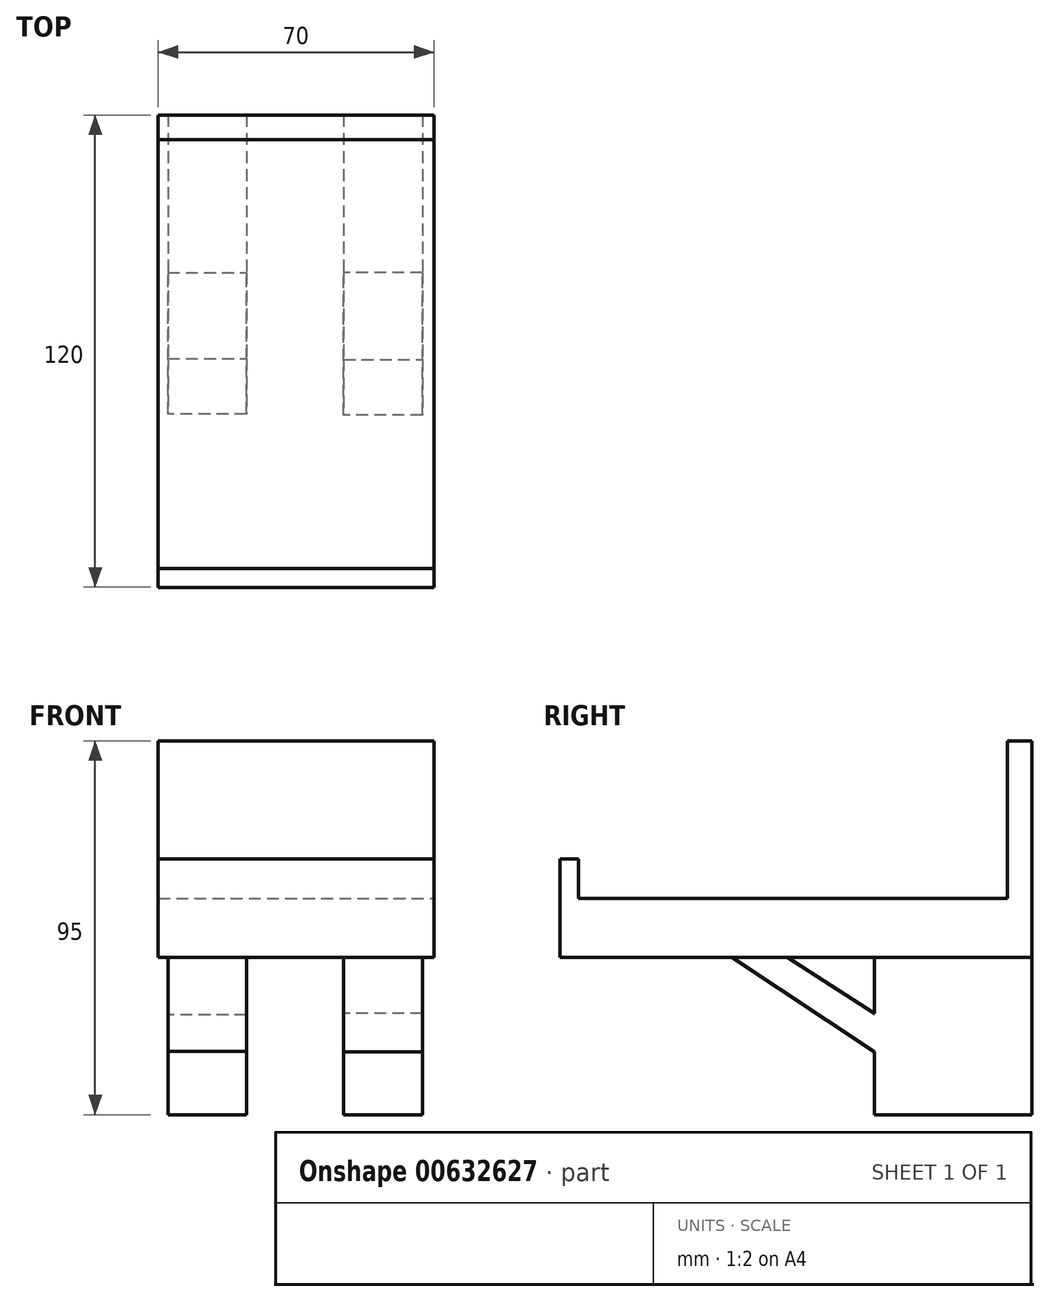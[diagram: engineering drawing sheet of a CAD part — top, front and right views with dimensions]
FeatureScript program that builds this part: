
annotation { "Feature Type Name" : "Feature", "Feature Type Description" : "" }
export const myFeature = defineFeature(function(context is Context, id is Id, definition is map)
    precondition{}
    {
        {
            var Q0;
            Q0=qCreatedBy(makeId("Top.planeOp"),FACE);
            var sketch = newSketch(context, id + "F0", { "sketchPlane" : qUnion([Q0])});
            skLineSegment(sketch, "E0.bottom", {"start": v(-70, 63.12) * mm, "end": v(0, 63.12) * mm});
            skLineSegment(sketch, "E0.top", {"start": v(-70, -56.88) * mm, "end": v(0, -56.88) * mm});
            skLineSegment(sketch, "E0.left", {"start": v(-70, 63.12) * mm, "end": v(-70, -56.88) * mm});
            skLineSegment(sketch, "E0.right", {"start": v(0, 63.12) * mm, "end": v(0, -56.88) * mm});
            skSolve(sketch);
        }
        {
            var Q0;
            Q0=makeQuery(id+"F0.imprint","IMPRINT",FACE,{"disambiguationData":[TD([[makeQuery(id+"F0.imprint","IMPRINT",EDGE,{"derivedFrom":sQuery(id+"F0.wireOp",EDGE,"E0.bottom")}),-1.0]])]});
            extrude(context, id + "F1", {"entities" : qUnion([Q0]), "depth" : 15 * mm, "offsetDistance" : 25 * mm});
        }
        {
            var Q0;
            Q0=makeQuery(id+"F1.opExtrude","CAP_FACE",FACE,{"disambiguationData":[OSD([sQuery(id+"F0.wireOp",EDGE,"E0.bottom"),sQuery(id+"F0.wireOp",EDGE,"E0.top"),sQuery(id+"F0.wireOp",EDGE,"E0.left"),sQuery(id+"F0.wireOp",EDGE,"E0.right")])],"isStart":true});
            var sketch = newSketch(context, id + "F2", { "sketchPlane" : qUnion([Q0])});
            skLineSegment(sketch, "E1.bottom", {"start": v(-67.57, -63.12) * mm, "end": v(-47.57, -63.12) * mm});
            skLineSegment(sketch, "E1.top", {"start": v(-67.57, -23.12) * mm, "end": v(-47.57, -23.12) * mm});
            skLineSegment(sketch, "E1.left", {"start": v(-67.57, -63.12) * mm, "end": v(-67.57, -23.12) * mm});
            skLineSegment(sketch, "E1.right", {"start": v(-47.57, -63.12) * mm, "end": v(-47.57, -23.12) * mm});
            skSolve(sketch);
        }
        {
            var Q0;
            Q0=makeQuery(id+"F2.imprint","IMPRINT",FACE,{"disambiguationData":[TD([[makeQuery(id+"F2.imprint","IMPRINT",EDGE,{"derivedFrom":sQuery(id+"F2.wireOp",EDGE,"E1.bottom")}),1.0]])]});
            extrude(context, id + "F3", {"entities" : qUnion([Q0]), "operationType" : NewBodyOperationType.ADD, "depth" : 40 * mm, "offsetDistance" : 25 * mm});
        }
        {
            var Q0;
            Q0=makeQuery(id+"F1.opExtrude","CAP_FACE",FACE,{"disambiguationData":[OSD([sQuery(id+"F0.wireOp",EDGE,"E0.bottom"),sQuery(id+"F0.wireOp",EDGE,"E0.top"),sQuery(id+"F0.wireOp",EDGE,"E0.left"),sQuery(id+"F0.wireOp",EDGE,"E0.right")])],"isStart":true});
            var sketch = newSketch(context, id + "F4", { "sketchPlane" : qUnion([Q0])});
            skLineSegment(sketch, "E2.bottom", {"start": v(-2.91, -63.12) * mm, "end": v(-22.91, -63.12) * mm});
            skLineSegment(sketch, "E2.top", {"start": v(-2.91, -23.12) * mm, "end": v(-22.91, -23.12) * mm});
            skLineSegment(sketch, "E2.left", {"start": v(-2.91, -63.12) * mm, "end": v(-2.91, -23.12) * mm});
            skLineSegment(sketch, "E2.right", {"start": v(-22.91, -63.12) * mm, "end": v(-22.91, -23.12) * mm});
            skSolve(sketch);
        }
        {
            var Q0;
            Q0=makeQuery(id+"F4.imprint","IMPRINT",FACE,{"disambiguationData":[TD([[makeQuery(id+"F4.imprint","IMPRINT",EDGE,{"derivedFrom":sQuery(id+"F4.wireOp",EDGE,"E2.bottom")}),1.0]])]});
            extrude(context, id + "F5", {"entities" : qUnion([Q0]), "operationType" : NewBodyOperationType.ADD, "depth" : 40 * mm, "offsetDistance" : 25 * mm});
        }
        {
            var Q0;
            Q0=makeQuery(id+"F5.opExtrude","SWEPT_FACE",FACE,{"disambiguationData":[OSD([sQuery(id+"F4.wireOp",EDGE,"E2.right")])]});
            var sketch = newSketch(context, id + "F6", { "sketchPlane" : qUnion([Q0])});
            skLineSegment(sketch, "E3", {"start": v(-29.44, -18.34) * mm, "end": v(14.37, 9.92) * mm});
            skLineSegment(sketch, "E4", {"start": v(14.37, 9.92) * mm, "end": v(28.08, 9.92) * mm});
            skLineSegment(sketch, "E5", {"start": v(28.08, 9.92) * mm, "end": v(-29.44, -28.22) * mm});
            skLineSegment(sketch, "E6", {"start": v(-29.44, -28.22) * mm, "end": v(-29.44, -18.34) * mm});
            skSolve(sketch);
        }
        {
            var Q0;
            {var subQ0=sQuery(id+"F6.wireOp",EDGE,"E4");Q0=makeQuery(id+"F6.imprint","IMPRINT",FACE,{"disambiguationData":[TD([[makeQuery(id+"F6.imprint","IMPRINT",EDGE,{"derivedFrom":subQ0}),-1.0]])]});}
            extrude(context, id + "F7", {"entities" : qUnion([Q0]), "operationType" : NewBodyOperationType.ADD, "oppositeDirection" : true, "depth" : 20 * mm, "offsetDistance" : 25 * mm});
        }
        {
            var Q0;
            Q0=makeQuery(id+"F3.opExtrude","SWEPT_FACE",FACE,{"disambiguationData":[OSD([sQuery(id+"F2.wireOp",EDGE,"E1.left")])]});
            var sketch = newSketch(context, id + "F8", { "sketchPlane" : qUnion([Q0])});
            skLineSegment(sketch, "E7", {"start": v(-32.98, -21.33) * mm, "end": v(12.87, 9.5) * mm});
            skLineSegment(sketch, "E8", {"start": v(12.87, 9.5) * mm, "end": v(23.59, 9.5) * mm});
            skLineSegment(sketch, "E9", {"start": v(23.59, 9.5) * mm, "end": v(27.16, 9.5) * mm});
            skLineSegment(sketch, "E10", {"start": v(27.16, 9.5) * mm, "end": v(-36, -32.42) * mm});
            skLineSegment(sketch, "E11", {"start": v(-36, -32.42) * mm, "end": v(-32.98, -21.33) * mm});
            skSolve(sketch);
        }
        {
            var Q0;
            {var subQ4=sQuery(id+"F8.wireOp",EDGE,"E8");Q0=makeQuery(id+"F8.imprint","IMPRINT",FACE,{"disambiguationData":[TD([[makeQuery(id+"F8.imprint","IMPRINT",EDGE,{"derivedFrom":subQ4}),-1.0]])]});}
            extrude(context, id + "F9", {"entities" : qUnion([Q0]), "operationType" : NewBodyOperationType.ADD, "oppositeDirection" : true, "depth" : 20 * mm, "offsetDistance" : 25 * mm});
        }
        {
            var Q0;
            Q0=makeQuery(id+"F1.opExtrude","CAP_FACE",FACE,{"disambiguationData":[OSD([sQuery(id+"F0.wireOp",EDGE,"E0.bottom"),sQuery(id+"F0.wireOp",EDGE,"E0.top"),sQuery(id+"F0.wireOp",EDGE,"E0.left"),sQuery(id+"F0.wireOp",EDGE,"E0.right")])],"isStart":false});
            var sketch = newSketch(context, id + "F10", { "sketchPlane" : qUnion([Q0])});
            skLineSegment(sketch, "E12.bottom", {"start": v(-70, -56.88) * mm, "end": v(0, -56.88) * mm});
            skLineSegment(sketch, "E12.top", {"start": v(-70, -52.16) * mm, "end": v(0, -52.16) * mm});
            skLineSegment(sketch, "E12.left", {"start": v(-70, -56.88) * mm, "end": v(-70, -52.16) * mm});
            skLineSegment(sketch, "E12.right", {"start": v(0, -56.88) * mm, "end": v(0, -52.16) * mm});
            skSolve(sketch);
        }
        {
            var Q0;
            Q0=makeQuery(id+"F10.imprint","IMPRINT",FACE,{"disambiguationData":[TD([[makeQuery(id+"F10.imprint","IMPRINT",EDGE,{"derivedFrom":sQuery(id+"F10.wireOp",EDGE,"E12.bottom")}),1.0]])]});
            extrude(context, id + "F11", {"entities" : qUnion([Q0]), "operationType" : NewBodyOperationType.ADD, "depth" : 10 * mm, "offsetDistance" : 25 * mm});
        }
        {
            var Q0;
            Q0=makeQuery(id+"F1.opExtrude","CAP_FACE",FACE,{"disambiguationData":[OSD([sQuery(id+"F0.wireOp",EDGE,"E0.bottom"),sQuery(id+"F0.wireOp",EDGE,"E0.top"),sQuery(id+"F0.wireOp",EDGE,"E0.left"),sQuery(id+"F0.wireOp",EDGE,"E0.right")])],"isStart":false});
            var sketch = newSketch(context, id + "F12", { "sketchPlane" : qUnion([Q0])});
            skLineSegment(sketch, "E13.bottom", {"start": v(-70, 63.12) * mm, "end": v(0, 63.12) * mm});
            skLineSegment(sketch, "E13.top", {"start": v(-70, 56.85) * mm, "end": v(0, 56.85) * mm});
            skLineSegment(sketch, "E13.left", {"start": v(-70, 63.12) * mm, "end": v(-70, 56.85) * mm});
            skLineSegment(sketch, "E13.right", {"start": v(0, 63.12) * mm, "end": v(0, 56.85) * mm});
            skSolve(sketch);
        }
        {
            var Q0;
            Q0=makeQuery(id+"F12.imprint","IMPRINT",FACE,{"disambiguationData":[TD([[makeQuery(id+"F12.imprint","IMPRINT",EDGE,{"derivedFrom":sQuery(id+"F12.wireOp",EDGE,"E13.bottom")}),-1.0]])]});
            extrude(context, id + "F13", {"entities" : qUnion([Q0]), "operationType" : NewBodyOperationType.ADD, "depth" : 40 * mm, "offsetDistance" : 25 * mm});
        }
    });
